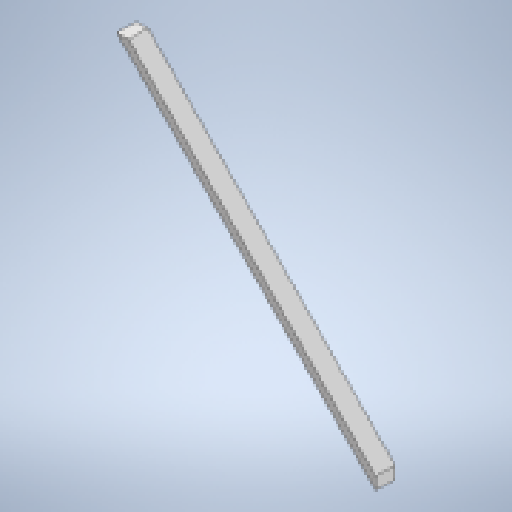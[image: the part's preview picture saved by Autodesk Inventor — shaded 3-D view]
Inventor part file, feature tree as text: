
AUTODESK INVENTOR PART (.ipt)
format: ipt  version: 2025.1 (Build 291241020, 241B)  size: 136,192 bytes
history: native  units: in
note: dims shown in document units (in); Inventor stores cm internally (conversion verified against a paired STEP export)
features: other x4, reference x2, extrude x1, sketch x1
ambient origin geometry x8: Origin, YZ Plane, XZ Plane, XY Plane, X Axis, Y Axis, Z Axis, Center Point
bodies: Solid1 (feature_tree)
feature tree (8):
  extrude  "Extrusion1"  Depth=3.5in TaperAngle=0.0deg
  sketch  "Sketch1"  dims[d0=1.5in d1=3.5in d2=0.0in]
  reference  "Reference1"
  reference  "Reference2"
  other  "<userpath>\Documents\Tburn24\F_Legs2\F_Legs2.iam"
  other  "F_Legs2.iam"
  other  "4x2x4:5"
  other  "8'x2x4:3"
